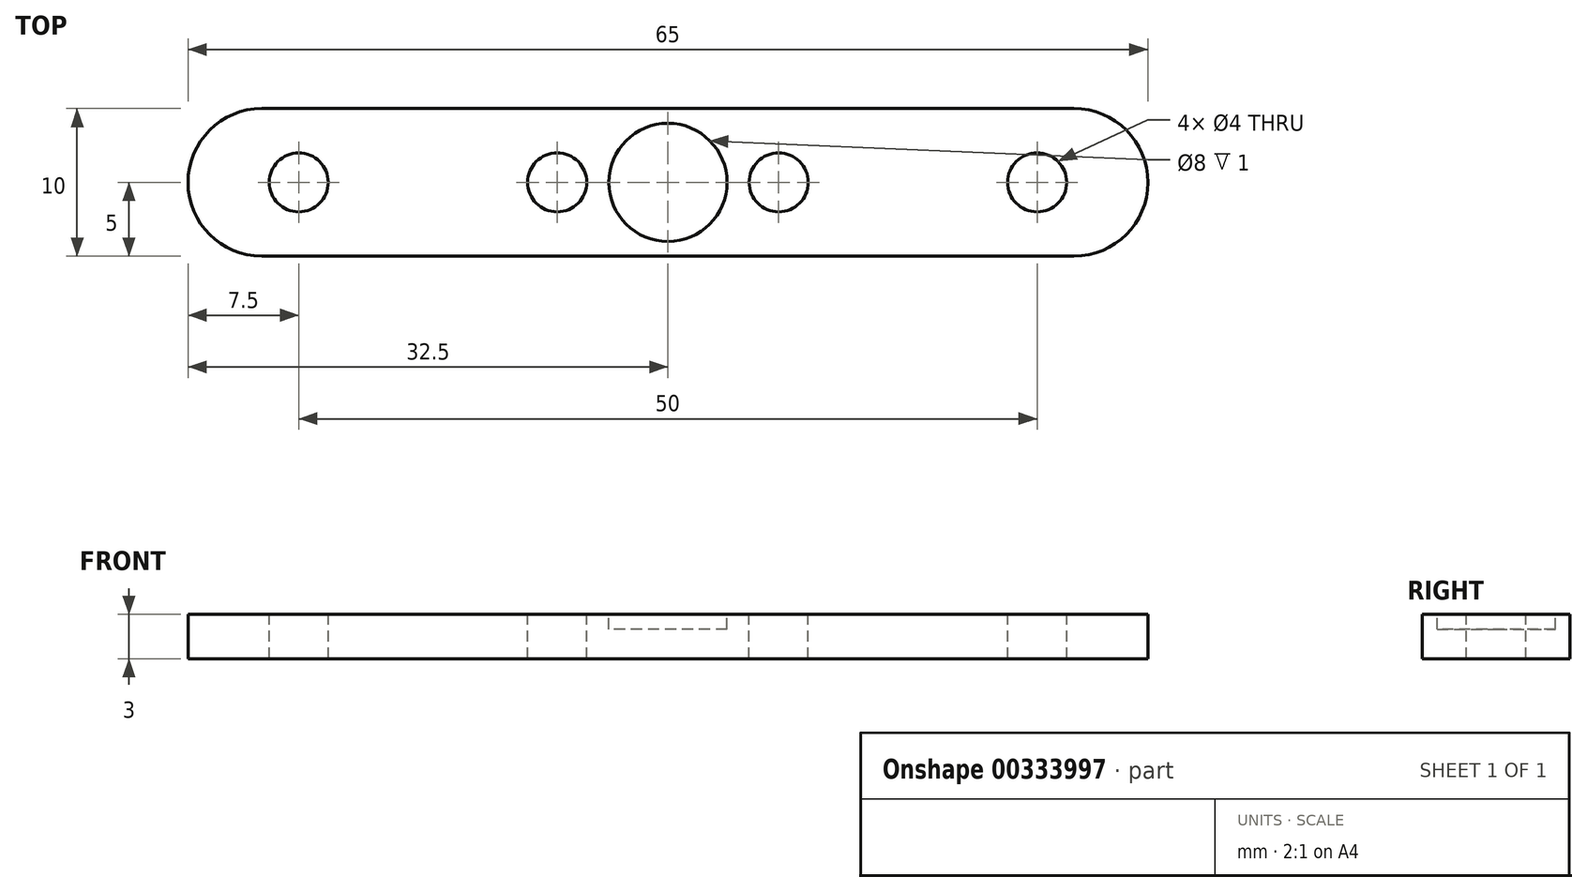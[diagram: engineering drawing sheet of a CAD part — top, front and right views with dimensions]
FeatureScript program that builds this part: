
annotation { "Feature Type Name" : "Feature", "Feature Type Description" : "" }
export const myFeature = defineFeature(function(context is Context, id is Id, definition is map)
    precondition{}
    {
        {
            var Q0;
            Q0=qCreatedBy(makeId("Top.planeOp"),FACE);
            var sketch = newSketch(context, id + "F0", { "sketchPlane" : qUnion([Q0])});
            skLineSegment(sketch, "E0.bottom", {"start": v(32.5, -5) * mm, "end": v(-32.5, -5) * mm});
            skLineSegment(sketch, "E0.top", {"start": v(32.5, 5) * mm, "end": v(-32.5, 5) * mm});
            skLineSegment(sketch, "E0.left", {"start": v(32.5, -5) * mm, "end": v(32.5, 5) * mm});
            skLineSegment(sketch, "E0.right", {"start": v(-32.5, -5) * mm, "end": v(-32.5, 5) * mm});
            skPoint(sketch, "E0.middle", {"position": v(0, 0) * mm});
            skSolve(sketch);
        }
        {
            var Q0;
            Q0 = qSketchRegion(id + "F0", true);
            extrude(context, id + "F1", {"entities" : qUnion([Q0]), "depth" : 3 * mm});
        }
        {
            var Q0;
            Q0=makeQuery(id+"F1.opExtrude","CAP_FACE",FACE,{"disambiguationData":[OSD([sQuery(id+"F0.wireOp",EDGE,"E0.bottom"),sQuery(id+"F0.wireOp",EDGE,"E0.top"),sQuery(id+"F0.wireOp",EDGE,"E0.left"),sQuery(id+"F0.wireOp",EDGE,"E0.right")])],"isStart":false});
            var sketch = newSketch(context, id + "F2", { "sketchPlane" : qUnion([Q0])});
            skCircle(sketch, "E1", {"center": v(0, 0) * mm, "radius": 4 * mm});
            skSolve(sketch);
        }
        {
            var Q0;
            Q0 = qSketchRegion(id + "F2", true);
            extrude(context, id + "F3", {"entities" : qUnion([Q0]), "operationType" : NewBodyOperationType.REMOVE, "oppositeDirection" : true, "depth" : 1 * mm});
        }
        {
            var Q0;
            Q0=makeQuery(id+"F1.opExtrude","CAP_FACE",FACE,{"disambiguationData":[OSD([sQuery(id+"F0.wireOp",EDGE,"E0.bottom"),sQuery(id+"F0.wireOp",EDGE,"E0.top"),sQuery(id+"F0.wireOp",EDGE,"E0.left"),sQuery(id+"F0.wireOp",EDGE,"E0.right")])],"isStart":false});
            var sketch = newSketch(context, id + "F4", { "sketchPlane" : qUnion([Q0])});
            skCircle(sketch, "E2", {"center": v(-7.5, 0) * mm, "radius": 2 * mm});
            skCircle(sketch, "E3", {"center": v(7.5, 0) * mm, "radius": 2 * mm});
            skCircle(sketch, "E4", {"center": v(-25, 0) * mm, "radius": 2 * mm});
            skCircle(sketch, "E5", {"center": v(25, 0) * mm, "radius": 2 * mm});
            skSolve(sketch);
        }
        {
            var Q0;
            Q0 = qSketchRegion(id + "F4", true);
            extrude(context, id + "F5", {"entities" : qUnion([Q0]), "operationType" : NewBodyOperationType.REMOVE, "oppositeDirection" : true, "depth" : 25 * mm});
        }
        {
            var Q0;
            Q0=makeQuery(id+"F1.opExtrude","SWEPT_EDGE",EDGE,{"disambiguationData":[OSD([sQuery(id+"F0.wireOp",EDGE,"E0.bottom"),sQuery(id+"F0.wireOp",EDGE,"E0.right")])]});
            var Q1;
            Q1=makeQuery(id+"F1.opExtrude","SWEPT_EDGE",EDGE,{"disambiguationData":[OSD([sQuery(id+"F0.wireOp",EDGE,"E0.top"),sQuery(id+"F0.wireOp",EDGE,"E0.right")])]});
            var Q2;
            Q2=makeQuery(id+"F1.opExtrude","SWEPT_EDGE",EDGE,{"disambiguationData":[OSD([sQuery(id+"F0.wireOp",EDGE,"E0.bottom"),sQuery(id+"F0.wireOp",EDGE,"E0.left")])]});
            var Q3;
            Q3=makeQuery(id+"F1.opExtrude","SWEPT_EDGE",EDGE,{"disambiguationData":[OSD([sQuery(id+"F0.wireOp",EDGE,"E0.top"),sQuery(id+"F0.wireOp",EDGE,"E0.left")])]});
            fillet(context, id + "F6", {"entities" : qUnion([Q0, Q1, Q2, Q3]), "radius" : 5 * mm, "tangentPropagation" : true, "allowEdgeOverflow" : false});
        }
    });
